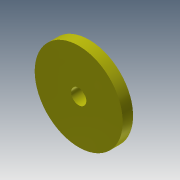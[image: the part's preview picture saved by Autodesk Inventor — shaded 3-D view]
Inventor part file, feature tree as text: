
AUTODESK INVENTOR PART (.ipt)
format: ipt  version: 2013 (Build 170138000, 138)  size: 109,056 bytes
history: native  units: mm
features: extrude x5, sketch x5
ambient origin geometry x8: Origin, YZ Plane, XZ Plane, XY Plane, X Axis, Y Axis, Z Axis, Center Point
bodies: Solid1 (feature_tree)
feature tree (10):
  extrude  "Extrusion1"  Depth=6.0mm
  extrude  "Extrusion2"  Depth=29.0mm
  extrude  "Extrusion3"  Depth=1.0mm TaperAngle=0.0deg
  extrude  "Extrusion4"  Depth=3.8mm TaperAngle=0.0deg
  extrude  "Extrusion5"  Depth=3.8mm TaperAngle=0.0deg
  sketch  "Sketch1"  dims[d0=34.65mm d1=6.0mm]
  sketch  "Sketch2"  dims[d2=4.1mm d3=0.0mm d4=29.0mm]
  sketch  "Sketch3"  dims[d5=1.0mm d6=0.0mm d7=1.0mm d8=0.0mm]
  sketch  "Sketch4"  dims[d9=10.0mm d10=3.8mm d11=0.0mm]
  sketch  "Sketch5"  dims[d12=6.0mm d13=3.8mm d14=0.0mm]
